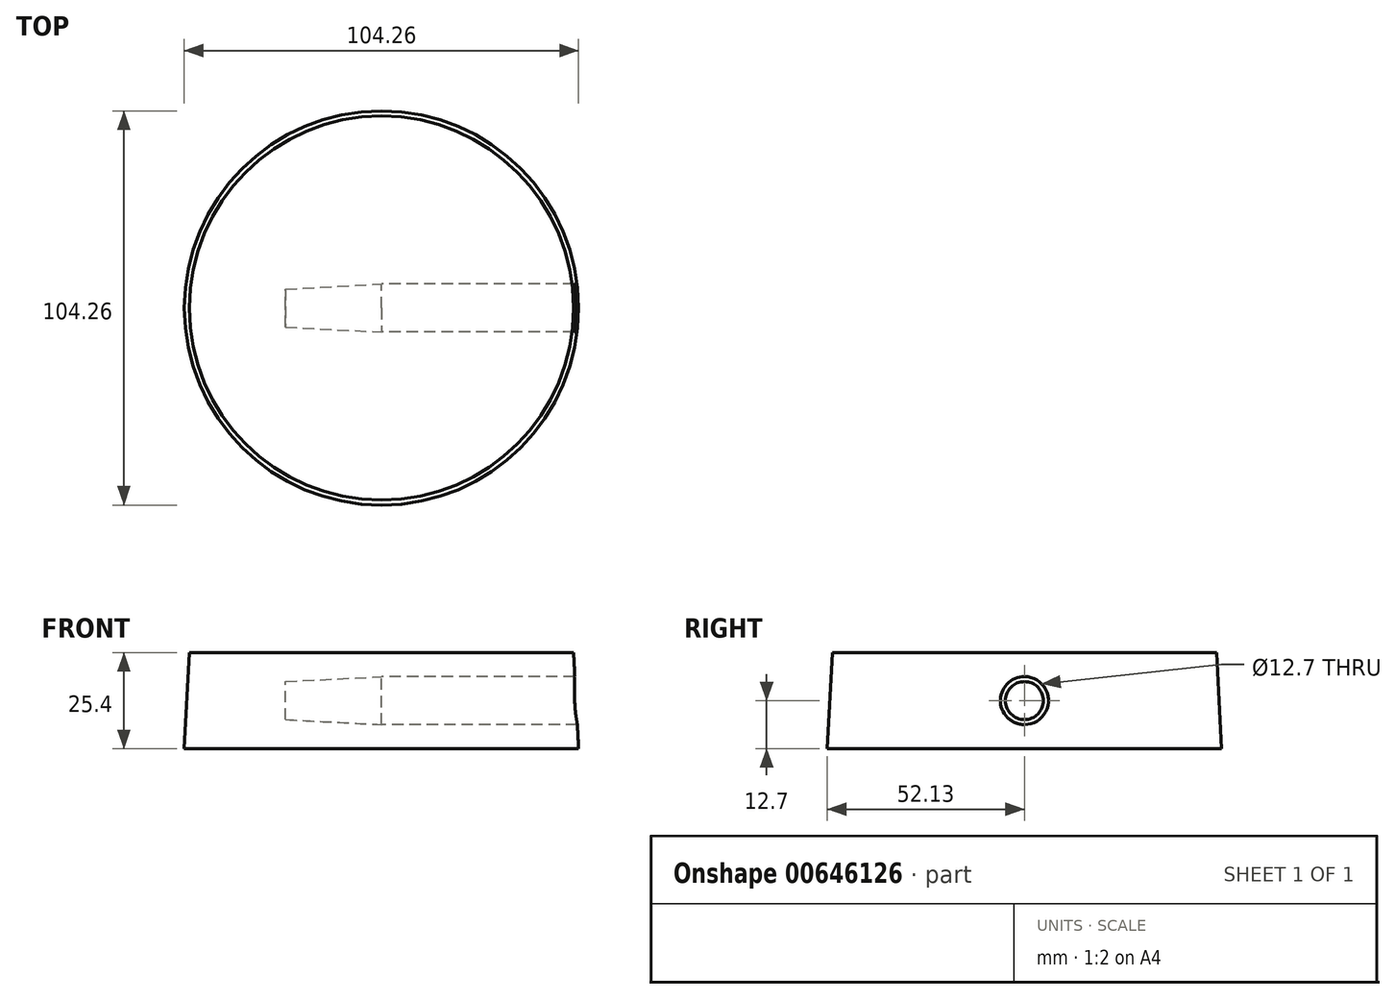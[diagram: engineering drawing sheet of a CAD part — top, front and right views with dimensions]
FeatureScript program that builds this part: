
annotation { "Feature Type Name" : "Feature", "Feature Type Description" : "" }
export const myFeature = defineFeature(function(context is Context, id is Id, definition is map)
    precondition{}
    {
        {
            var Q0;
            Q0=qCreatedBy(makeId("Top.planeOp"),FACE);
            var sketch = newSketch(context, id + "F0", { "sketchPlane" : qUnion([Q0])});
            skCircle(sketch, "E0", {"center": v(0, 0) * mm, "radius": 50.8 * mm});
            skSolve(sketch);
        }
        {
            var Q0;
            Q0 = qSketchRegion(id + "F0", true);
            extrude(context, id + "F1", {"entities" : qUnion([Q0]), "oppositeDirection" : true, "depth" : 25.4 * mm, "offsetDistance" : 25.4 * mm, "hasDraft" : true, "draftAngle" : 3 * degree});
        }
        {
            var Q0;
            Q0=qCreatedBy(makeId("Right.planeOp"),FACE);
            var sketch = newSketch(context, id + "F2", { "sketchPlane" : qUnion([Q0])});
            skCircle(sketch, "E1", {"center": v(0, -12.7) * mm, "radius": 6.35 * mm});
            skSolve(sketch);
        }
        {
            var Q0;
            Q0 = qSketchRegion(id + "F2", true);
            extrude(context, id + "F3", {"entities" : qUnion([Q0]), "operationType" : NewBodyOperationType.REMOVE, "endBound" : BoundingType.UP_TO_NEXT, "depth" : 25.4 * mm, "offsetDistance" : 25.4 * mm, "hasSecondDirection" : true, "secondDirectionOppositeDirection" : true, "secondDirectionDepth" : 25.4 * mm, "hasSecondDirectionDraft" : true, "secondDirectionDraftAngle" : 3 * degree, "secondDirectionDraftPullDirection" : true});
        }
    });
